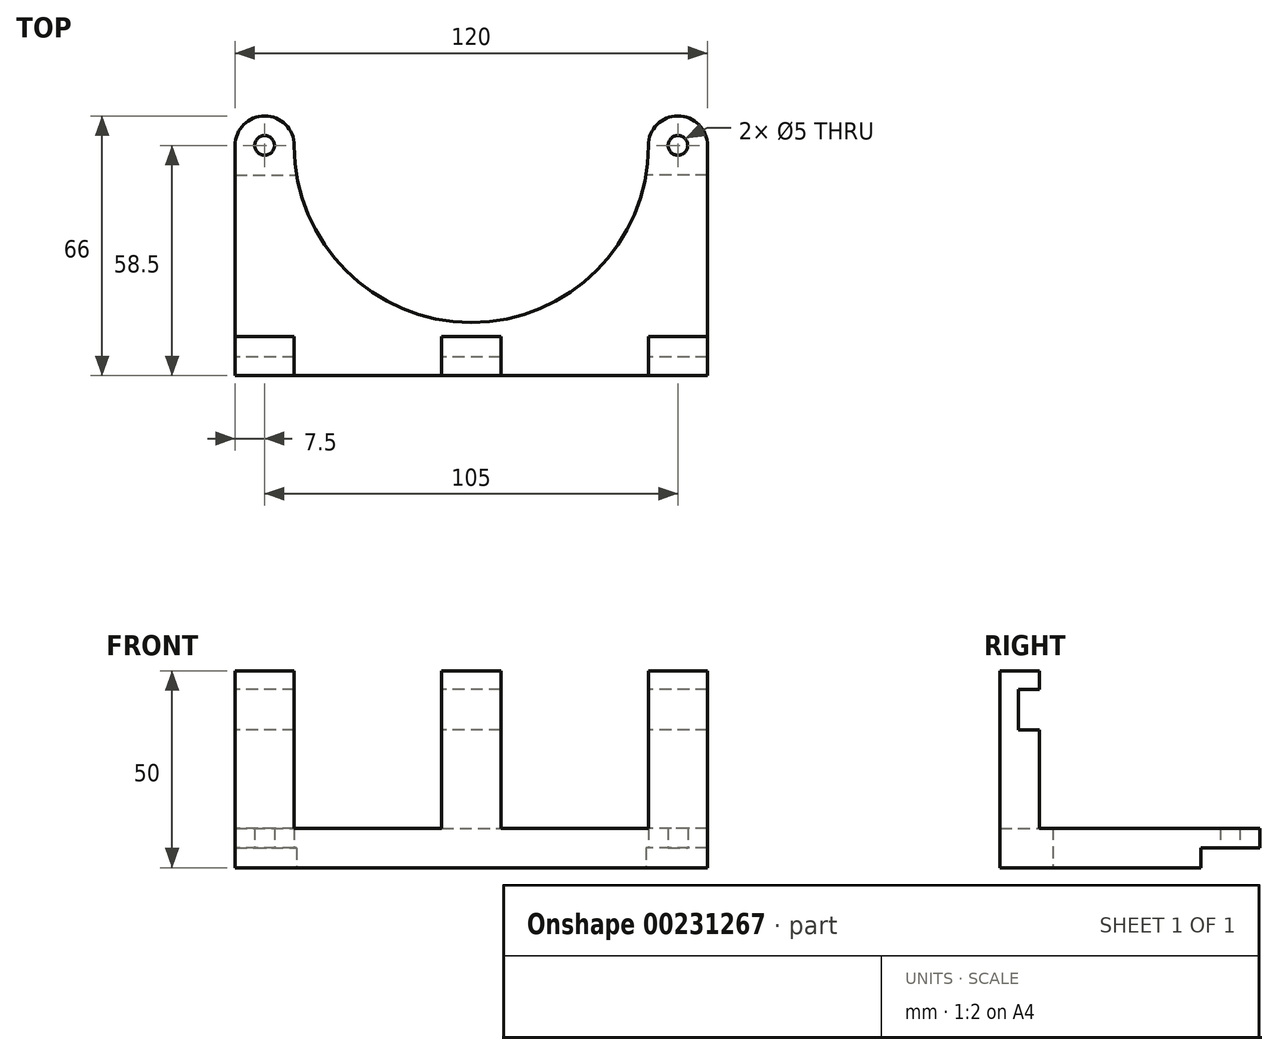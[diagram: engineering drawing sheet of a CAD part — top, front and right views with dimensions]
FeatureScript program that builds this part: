
annotation { "Feature Type Name" : "Feature", "Feature Type Description" : "" }
export const myFeature = defineFeature(function(context is Context, id is Id, definition is map)
    precondition{}
    {
        {
            var Q0;
            Q0=qCreatedBy(makeId("Top.planeOp"),FACE);
            var sketch = newSketch(context, id + "F0", { "sketchPlane" : qUnion([Q0])});
            skLineSegment(sketch, "E0.bottom", {"start": v(0, 0) * mm, "end": v(120, 0) * mm, "construction": true});
            skLineSegment(sketch, "E0.top", {"start": v(0, 120) * mm, "end": v(120, 120) * mm, "construction": true});
            skLineSegment(sketch, "E0.left", {"start": v(0, 0) * mm, "end": v(0, 120) * mm, "construction": true});
            skLineSegment(sketch, "E0.right", {"start": v(120, 0) * mm, "end": v(120, 120) * mm, "construction": true});
            skLineSegment(sketch, "E1.bottom", {"start": v(7.5, 7.5) * mm, "end": v(112.5, 7.5) * mm, "construction": true});
            skLineSegment(sketch, "E1.top", {"start": v(7.5, 112.5) * mm, "end": v(112.5, 112.5) * mm, "construction": true});
            skLineSegment(sketch, "E1.left", {"start": v(7.5, 7.5) * mm, "end": v(7.5, 112.5) * mm, "construction": true});
            skLineSegment(sketch, "E1.right", {"start": v(112.5, 7.5) * mm, "end": v(112.5, 112.5) * mm, "construction": true});
            skCircle(sketch, "E2", {"center": v(7.5, 7.5) * mm, "radius": 2.5 * mm});
            skCircle(sketch, "E3", {"center": v(112.5, 7.5) * mm, "radius": 2.5 * mm});
            skArc(sketch, "E4", {"start": v(15, 7.5) * mm, "mid": v(7.5, 15) * mm, "end": v(0, 7.5) * mm});
            skArc(sketch, "E5", {"start": v(120, 7.5) * mm, "mid": v(112.5, 15) * mm, "end": v(105, 7.5) * mm});
            skLineSegment(sketch, "E6", {"start": v(0, 7.5) * mm, "end": v(0, -51) * mm});
            skLineSegment(sketch, "E7", {"start": v(120, 7.5) * mm, "end": v(120, -51) * mm});
            skLineSegment(sketch, "E8", {"start": v(120, -51) * mm, "end": v(0, -51) * mm});
            skArc(sketch, "E9", {"start": v(15, 7.5) * mm, "mid": v(60, -37.5) * mm, "end": v(105, 7.5) * mm});
            skSolve(sketch);
        }
        {
            var Q0;
            Q0 = qSketchRegion(id + "F0", true);
            extrude(context, id + "F1", {"entities" : qUnion([Q0]), "depth" : 10 * mm});
        }
        {
            var Q0;
            Q0=makeQuery(id+"F1.opExtrude","CAP_FACE",FACE,{"disambiguationData":[OSD([sQuery(id+"F0.wireOp",EDGE,"E2"),sQuery(id+"F0.wireOp",EDGE,"E3"),sQuery(id+"F0.wireOp",EDGE,"E4"),sQuery(id+"F0.wireOp",EDGE,"E5"),sQuery(id+"F0.wireOp",EDGE,"E6"),sQuery(id+"F0.wireOp",EDGE,"E7"),sQuery(id+"F0.wireOp",EDGE,"E8"),sQuery(id+"F0.wireOp",EDGE,"E9")])],"isStart":true});
            var sketch = newSketch(context, id + "F2", { "sketchPlane" : qUnion([Q0])});
            skArc(sketch, "E10.0", {"start": v(15, -7.5) * mm, "mid": v(7.5, -15) * mm, "end": v(0, -7.5) * mm});
            skArc(sketch, "E11.0", {"start": v(120, -7.5) * mm, "mid": v(112.5, -15) * mm, "end": v(105, -7.5) * mm});
            skLineSegment(sketch, "E12", {"start": v(0, 0) * mm, "end": v(0, -7.5) * mm});
            skLineSegment(sketch, "E13", {"start": v(0, 0) * mm, "end": v(15.63, 0) * mm});
            skLineSegment(sketch, "E14", {"start": v(120, 0) * mm, "end": v(120, -7.5) * mm});
            skLineSegment(sketch, "E15", {"start": v(120, 0) * mm, "end": v(104.37, 0) * mm});
            skArc(sketch, "E16.0", {"start": v(15, -7.5) * mm, "mid": v(15.16, -3.74) * mm, "end": v(15.63, 0) * mm});
            skArc(sketch, "E17.trimOffspring", {"start": v(104.37, 0) * mm, "mid": v(15.16, -11.26) * mm, "end": v(105, -7.5) * mm});
            skSolve(sketch);
        }
        {
            var Q0;
            Q0 = qSketchRegion(id + "F2", true);
            extrude(context, id + "F3", {"entities" : qUnion([Q0]), "operationType" : NewBodyOperationType.REMOVE, "oppositeDirection" : true, "depth" : 5 * mm});
        }
        {
            var Q0;
            Q0=makeQuery(id+"F1.opExtrude","CAP_FACE",FACE,{"disambiguationData":[OSD([sQuery(id+"F0.wireOp",EDGE,"E2"),sQuery(id+"F0.wireOp",EDGE,"E3"),sQuery(id+"F0.wireOp",EDGE,"E4"),sQuery(id+"F0.wireOp",EDGE,"E5"),sQuery(id+"F0.wireOp",EDGE,"E6"),sQuery(id+"F0.wireOp",EDGE,"E7"),sQuery(id+"F0.wireOp",EDGE,"E8"),sQuery(id+"F0.wireOp",EDGE,"E9")])],"isStart":false});
            var sketch = newSketch(context, id + "F4", { "sketchPlane" : qUnion([Q0])});
            skLineSegment(sketch, "E18.bottom", {"start": v(0, -51) * mm, "end": v(15, -51) * mm});
            skLineSegment(sketch, "E18.top", {"start": v(0, -41) * mm, "end": v(15, -41) * mm});
            skLineSegment(sketch, "E18.left", {"start": v(0, -51) * mm, "end": v(0, -41) * mm});
            skLineSegment(sketch, "E18.right", {"start": v(15, -51) * mm, "end": v(15, -41) * mm});
            skPoint(sketch, "E19.oppositeSnap0", {"position": v(7.5, -41) * mm});
            skLineSegment(sketch, "E19.bottom", {"start": v(120, -51) * mm, "end": v(105, -51) * mm});
            skLineSegment(sketch, "E19.top", {"start": v(120, -41) * mm, "end": v(105, -41) * mm});
            skLineSegment(sketch, "E19.left", {"start": v(120, -51) * mm, "end": v(120, -41) * mm});
            skLineSegment(sketch, "E19.right", {"start": v(105, -51) * mm, "end": v(105, -41) * mm});
            skLineSegment(sketch, "E20.bottom", {"start": v(52.5, -51) * mm, "end": v(67.5, -51) * mm});
            skLineSegment(sketch, "E20.top", {"start": v(52.5, -41) * mm, "end": v(67.5, -41) * mm});
            skLineSegment(sketch, "E20.left", {"start": v(52.5, -51) * mm, "end": v(52.5, -41) * mm});
            skLineSegment(sketch, "E20.right", {"start": v(67.5, -51) * mm, "end": v(67.5, -41) * mm});
            skSolve(sketch);
        }
        {
            var Q0;
            Q0 = qSketchRegion(id + "F4", true);
            extrude(context, id + "F5", {"entities" : qUnion([Q0]), "operationType" : NewBodyOperationType.ADD, "depth" : 40 * mm});
        }
        {
            var Q0;
            Q0=makeQuery(id+"F5.boolean.opBoolean","MERGE",FACE,{"derivedFrom":[makeQuery(id+"F1.opExtrude","SWEPT_FACE",FACE,{"disambiguationData":[OSD([sQuery(id+"F0.wireOp",EDGE,"E6")])]}),makeQuery(id+"F5.opExtrude","SWEPT_FACE",FACE,{"disambiguationData":[OSD([sQuery(id+"F4.wireOp",EDGE,"E18.left")])]})]});
            var sketch = newSketch(context, id + "F6", { "sketchPlane" : qUnion([Q0])});
            skLineSegment(sketch, "E21.bottom", {"start": v(41, 45.3) * mm, "end": v(46.3, 45.3) * mm});
            skLineSegment(sketch, "E21.top", {"start": v(41, 35) * mm, "end": v(46.3, 35) * mm});
            skLineSegment(sketch, "E21.left", {"start": v(41, 45.3) * mm, "end": v(41, 35) * mm});
            skLineSegment(sketch, "E21.right", {"start": v(46.3, 45.3) * mm, "end": v(46.3, 35) * mm});
            skSolve(sketch);
        }
        {
            var Q0;
            Q0 = qSketchRegion(id + "F6", true);
            extrude(context, id + "F7", {"entities" : qUnion([Q0]), "operationType" : NewBodyOperationType.REMOVE, "endBound" : BoundingType.THROUGH_ALL, "oppositeDirection" : true, "depth" : 25 * mm});
        }
    });
